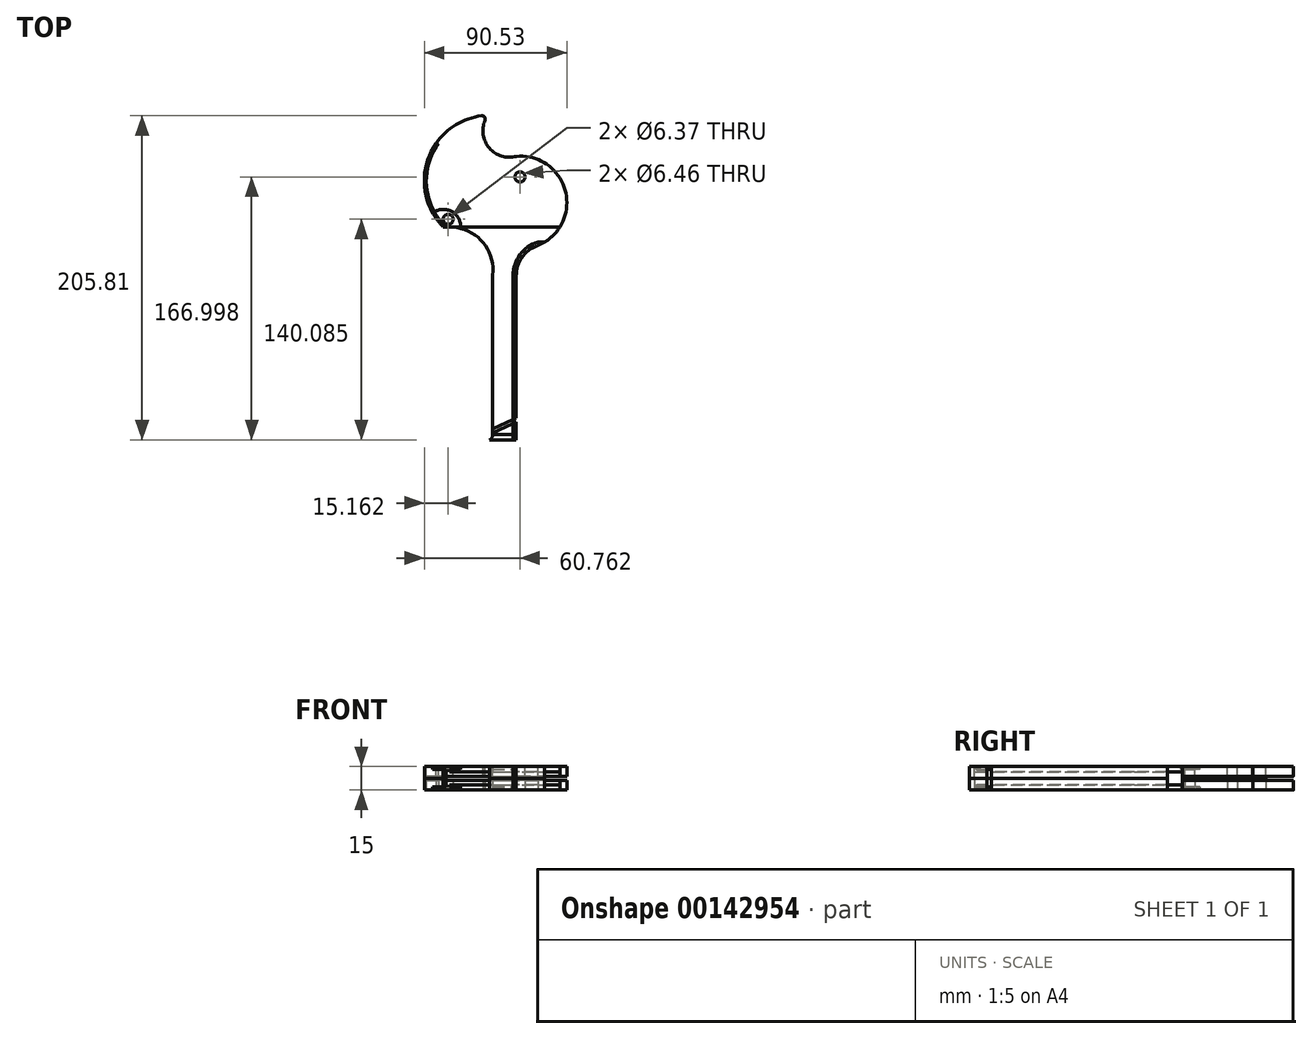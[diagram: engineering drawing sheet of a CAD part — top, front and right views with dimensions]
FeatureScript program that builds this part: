
annotation { "Feature Type Name" : "Feature", "Feature Type Description" : "" }
export const myFeature = defineFeature(function(context is Context, id is Id, definition is map)
    precondition{}
    {
        {
            var Q0;
            Q0=qCreatedBy(makeId("Top.planeOp"),FACE);
            var sketch = newSketch(context, id + "F0", { "sketchPlane" : qUnion([Q0])});
            skLineSegment(sketch, "E0", {"start": v(8.8, -17.92) * mm, "end": v(8.8, -59.13) * mm});
            skArc(sketch, "E1", {"start": v(21.81, 0.82) * mm, "mid": v(40.21, 34.88) * mm, "end": v(8.92, 57.68) * mm});
            skArc(sketch, "E2", {"start": v(-11.05, 80.69) * mm, "mid": v(-8.27, 62.97) * mm, "end": v(8.86, 57.67) * mm});
            skArc(sketch, "E3", {"start": v(-13.14, 83.45) * mm, "mid": v(-47.3, 55.79) * mm, "end": v(-37.55, 12.92) * mm});
            skArc(sketch, "E4", {"start": v(-6.16, -17.65) * mm, "mid": v(-12.98, 3.75) * mm, "end": v(-33.49, 12.92) * mm});
            skLineSegment(sketch, "E5", {"start": v(-6.2, -18.21) * mm, "end": v(-6.2, -119.09) * mm});
            skArc(sketch, "E6", {"start": v(-8.08, -122.34) * mm, "mid": v(-6.7, -120.97) * mm, "end": v(-6.2, -119.09) * mm});
            skLineSegment(sketch, "E7", {"start": v(-8.08, -122.34) * mm, "end": v(8.8, -122.34) * mm});
            skLineSegment(sketch, "E8", {"start": v(8.8, -122.34) * mm, "end": v(8.8, -59.13) * mm});
            skArc(sketch, "E9.filletArc", {"start": v(8.92, 57.68) * mm, "mid": v(8.9, 57.68) * mm, "end": v(8.86, 57.67) * mm});
            skCircle(sketch, "E10", {"center": v(11.17, 44.66) * mm, "radius": 3.23 * mm});
            skCircle(sketch, "E11", {"center": v(-34.43, 17.74) * mm, "radius": 3.19 * mm});
            skPoint(sketch, "E12.visualSharp", {"position": v(8.8, -0.92) * mm});
            skArc(sketch, "E12.filletArc", {"start": v(21.81, 0.82) * mm, "mid": v(12.38, -6.52) * mm, "end": v(8.8, -17.92) * mm});
            skPoint(sketch, "E13.visualSharp", {"position": v(-9.36, 83.75) * mm});
            skArc(sketch, "E13.filletArc", {"start": v(-11.05, 80.69) * mm, "mid": v(-11.3, 82.67) * mm, "end": v(-13.14, 83.45) * mm});
            skPoint(sketch, "E14.visualSharp", {"position": v(-6.2, -17.92) * mm});
            skArc(sketch, "E14.filletArc", {"start": v(-6.16, -17.65) * mm, "mid": v(-6.18, -17.93) * mm, "end": v(-6.2, -18.21) * mm});
            skLineSegment(sketch, "E15", {"start": v(-37.55, 12.92) * mm, "end": v(-33.49, 12.92) * mm});
            skLineSegment(sketch, "E16", {"start": v(-37.55, 12.92) * mm, "end": v(36.55, 12.92) * mm});
            skLineSegment(sketch, "E17.0", {"start": v(6.75, -122.34) * mm, "end": v(6.75, -59.13) * mm});
            skLineSegment(sketch, "E17.1", {"start": v(6.75, -17.92) * mm, "end": v(6.75, -59.13) * mm});
            skArc(sketch, "E17.2", {"start": v(22.5, 3.22) * mm, "mid": v(11.12, -4.74) * mm, "end": v(6.75, -17.92) * mm});
            skLineSegment(sketch, "E18", {"start": v(22.5, 3.22) * mm, "end": v(26.77, 3.22) * mm});
            skArc(sketch, "E19", {"start": v(-40.58, 65.88) * mm, "mid": v(-48.16, 38.5) * mm, "end": v(-35.8, 12.92) * mm});
            skLineSegment(sketch, "E20", {"start": v(-40.58, 65.88) * mm, "end": v(-42.18, 65.88) * mm});
            skLineSegment(sketch, "E21", {"start": v(-6.2, -119.09) * mm, "end": v(6.75, -119.09) * mm});
            skSolve(sketch);
        }
        {
            var Q0;
            Q0=makeQuery(id+"F0.imprint","IMPRINT",FACE,{"disambiguationData":[TD([[makeQuery(id+"F0.imprint","IMPRINT",EDGE,{"derivedFrom":sQuery(id+"F0.wireOp",EDGE,"E0")}),-1.0]])]});
            extrude(context, id + "F1", {"entities" : qUnion([Q0]), "oppositeDirection" : true, "depth" : 7.5 * mm});
        }
        {
            var Q0;
            {var subQ0=sQuery(id+"F0.wireOp",EDGE,"E21");Q0=makeQuery(id+"F0.imprint","IMPRINT",FACE,{"disambiguationData":[TD([[makeQuery(id+"F0.imprint","IMPRINT",EDGE,{"derivedFrom":subQ0}),-1.0]])]});}
            extrude(context, id + "F2", {"entities" : qUnion([Q0]), "oppositeDirection" : true, "depth" : 7.5 * mm});
        }
        {
            var Q0;
            {var subQ1=sQuery(id+"F0.wireOp",EDGE,"E4");Q0=makeQuery(id+"F0.imprint","IMPRINT",FACE,{"disambiguationData":[TD([[makeQuery(id+"F0.imprint","IMPRINT",EDGE,{"derivedFrom":subQ1}),-1.0]])]});}
            extrude(context, id + "F3", {"entities" : qUnion([Q0]), "oppositeDirection" : true, "depth" : 3.33 * mm});
        }
        {
            var Q0;
            Q0=makeQuery(id+"F0.imprint","IMPRINT",FACE,{"disambiguationData":[TD([[makeQuery(id+"F0.imprint","IMPRINT",EDGE,{"derivedFrom":sQuery(id+"F0.wireOp",EDGE,"E2")}),-1.0]])]});
            extrude(context, id + "F4", {"entities" : qUnion([Q0]), "oppositeDirection" : true, "depth" : 6.14 * mm});
        }
        {
            var Q0;
            {var subQ4=sQuery(id+"F0.wireOp",EDGE,"E20");Q0=makeQuery(id+"F0.imprint","IMPRINT",FACE,{"disambiguationData":[TD([[makeQuery(id+"F0.imprint","IMPRINT",EDGE,{"derivedFrom":subQ4}),1.0]])]});}
            extrude(context, id + "F5", {"entities" : qUnion([Q0]), "oppositeDirection" : true, "depth" : 7.5 * mm});
        }
        {
            var Q0;
            Q0=makeQuery(id+"F1.opExtrude","CAP_FACE",FACE,{"disambiguationData":[OSD([sQuery(id+"F0.wireOp",EDGE,"E0"),sQuery(id+"F0.wireOp",EDGE,"E1"),sQuery(id+"F0.wireOp",EDGE,"E7"),sQuery(id+"F0.wireOp",EDGE,"E8"),sQuery(id+"F0.wireOp",EDGE,"E12.filletArc"),sQuery(id+"F0.wireOp",EDGE,"E17.0"),sQuery(id+"F0.wireOp",EDGE,"E17.1"),sQuery(id+"F0.wireOp",EDGE,"E17.2"),sQuery(id+"F0.wireOp",EDGE,"E18")])],"isStart":false});
            cPlane(context, id + "F6", {"entities" : qUnion([Q0]), "cplaneType" : CPlaneType.OFFSET, "offset" : 0 * mm, "width" : 150 * mm, "height" : 150 * mm});
        }
        {
            var Q0;
            Q0=makeQuery(id+"F3.opExtrude","CAP_FACE",FACE,{"disambiguationData":[OSD([sQuery(id+"F0.wireOp",EDGE,"E1"),sQuery(id+"F0.wireOp",EDGE,"E4"),sQuery(id+"F0.wireOp",EDGE,"E5"),sQuery(id+"F0.wireOp",EDGE,"E14.filletArc"),sQuery(id+"F0.wireOp",EDGE,"E16"),sQuery(id+"F0.wireOp",EDGE,"E17.0"),sQuery(id+"F0.wireOp",EDGE,"E17.1"),sQuery(id+"F0.wireOp",EDGE,"E17.2"),sQuery(id+"F0.wireOp",EDGE,"E18"),sQuery(id+"F0.wireOp",EDGE,"E21")])],"isStart":true});
            var sketch = newSketch(context, id + "F7", { "sketchPlane" : qUnion([Q0])});
            skLineSegment(sketch, "E22", {"start": v(-6.2, -118.1) * mm, "end": v(8.8, -111.11) * mm});
            skLineSegment(sketch, "E23", {"start": v(-6.2, -115.32) * mm, "end": v(8.8, -108.33) * mm});
            skLineSegment(sketch, "E24", {"start": v(8.8, -108.33) * mm, "end": v(8.8, -111.11) * mm});
            skSolve(sketch);
        }
        {
            var Q0;
            {var subQ0=sQuery(id+"F7.wireOp",EDGE,"E22");var subQ1=makeQuery(id+"F3.opExtrude","CAP_EDGE",EDGE,{"disambiguationData":[OSD([sQuery(id+"F0.wireOp",EDGE,"E5")])],"isStart":true});var subQ2=makeQuery(id+"F7.imprint","INTERSECT",VERTEX,{"derivedFrom":[subQ1,subQ0]});Q0=makeQuery(id+"F7.imprint","IMPRINT",FACE,{"disambiguationData":[TD([[makeQuery(id+"F7.imprint","IMPRINT",EDGE,{"disambiguationData":[TD([[subQ2,1.0]])],"derivedFrom":subQ1}),1.0]])]});}
            var Q1;
            {var subQ0=sQuery(id+"F7.wireOp",EDGE,"E24");Q1=makeQuery(id+"F7.imprint","IMPRINT",FACE,{"disambiguationData":[TD([[makeQuery(id+"F7.imprint","IMPRINT",EDGE,{"derivedFrom":subQ0}),-1.0]])]});}
            extrude(context, id + "F8", {"entities" : qUnion([Q0, Q1]), "operationType" : NewBodyOperationType.REMOVE, "oppositeDirection" : true, "depth" : 2 * mm});
        }
        {
            var Q0;
            Q0=makeQuery(id+"F1.opExtrude","SWEPT_FACE",FACE,{"disambiguationData":[OSD([sQuery(id+"F0.wireOp",EDGE,"E0"),sQuery(id+"F0.wireOp",EDGE,"E8")])]});
            var sketch = newSketch(context, id + "F9", { "sketchPlane" : qUnion([Q0])});
            skLineSegment(sketch, "E25", {"start": v(-108.33, -2) * mm, "end": v(-108.33, -7.5) * mm});
            skLineSegment(sketch, "E26", {"start": v(-108.33, -7.5) * mm, "end": v(-111.11, -7.5) * mm});
            skLineSegment(sketch, "E27", {"start": v(-111.11, -7.5) * mm, "end": v(-111.11, -2) * mm});
            skSolve(sketch);
        }
        {
            var Q0;
            Q0=makeQuery(id+"F9.imprint","IMPRINT",FACE,{"disambiguationData":[TD([[makeQuery(id+"F9.imprint","IMPRINT",EDGE,{"derivedFrom":sQuery(id+"F9.wireOp",EDGE,"E25")}),-1.0]])]});
            extrude(context, id + "F10", {"entities" : qUnion([Q0]), "operationType" : NewBodyOperationType.REMOVE, "oppositeDirection" : true, "depth" : 2 * mm});
        }
        {
            var Q0;
            Q0=makeQuery(id+"F4.opExtrude","SWEPT_BODY",BODY,{"disambiguationData":[OSD([sQuery(id+"F0.wireOp",EDGE,"E1"),sQuery(id+"F0.wireOp",EDGE,"E2"),sQuery(id+"F0.wireOp",EDGE,"E3"),sQuery(id+"F0.wireOp",EDGE,"E9.filletArc"),sQuery(id+"F0.wireOp",EDGE,"E10"),sQuery(id+"F0.wireOp",EDGE,"E11"),sQuery(id+"F0.wireOp",EDGE,"E13.filletArc"),sQuery(id+"F0.wireOp",EDGE,"E16"),sQuery(id+"F0.wireOp",EDGE,"E19"),sQuery(id+"F0.wireOp",EDGE,"E20")])]});
            var Q1;
            Q1=makeQuery(id+"F3.opExtrude","SWEPT_BODY",BODY,{"disambiguationData":[OSD([sQuery(id+"F0.wireOp",EDGE,"E1"),sQuery(id+"F0.wireOp",EDGE,"E4"),sQuery(id+"F0.wireOp",EDGE,"E5"),sQuery(id+"F0.wireOp",EDGE,"E6"),sQuery(id+"F0.wireOp",EDGE,"E7"),sQuery(id+"F0.wireOp",EDGE,"E14.filletArc"),sQuery(id+"F0.wireOp",EDGE,"E16"),sQuery(id+"F0.wireOp",EDGE,"E17.0"),sQuery(id+"F0.wireOp",EDGE,"E17.1"),sQuery(id+"F0.wireOp",EDGE,"E17.2"),sQuery(id+"F0.wireOp",EDGE,"E18")])]});
            var Q2;
            Q2=makeQuery(id+"F1.opExtrude","SWEPT_BODY",BODY,{"disambiguationData":[OSD([sQuery(id+"F0.wireOp",EDGE,"E0"),sQuery(id+"F0.wireOp",EDGE,"E1"),sQuery(id+"F0.wireOp",EDGE,"E7"),sQuery(id+"F0.wireOp",EDGE,"E8"),sQuery(id+"F0.wireOp",EDGE,"E12.filletArc"),sQuery(id+"F0.wireOp",EDGE,"E17.0"),sQuery(id+"F0.wireOp",EDGE,"E17.1"),sQuery(id+"F0.wireOp",EDGE,"E17.2"),sQuery(id+"F0.wireOp",EDGE,"E18")])]});
            var Q3;
            Q3=makeQuery(id+"F5.opExtrude","SWEPT_BODY",BODY,{"disambiguationData":[OSD([sQuery(id+"F0.wireOp",EDGE,"E3"),sQuery(id+"F0.wireOp",EDGE,"E16"),sQuery(id+"F0.wireOp",EDGE,"E19"),sQuery(id+"F0.wireOp",EDGE,"E20")])]});
            var Q4;
            Q4=makeQuery(id+"F2.opExtrude","SWEPT_BODY",BODY,{"disambiguationData":[OSD([sQuery(id+"F0.wireOp",EDGE,"E6"),sQuery(id+"F0.wireOp",EDGE,"E7"),sQuery(id+"F0.wireOp",EDGE,"E17.0"),sQuery(id+"F0.wireOp",EDGE,"E21")])]});
            var Q5;
            Q5=qCreatedBy(id+"F6.planeOp",FACE);
            mirror(context, id + "F11", {"entities" : qUnion([Q0, Q1, Q2, Q3, Q4]), "mirrorPlane" : qUnion([Q5])});
        }
        {
            var Q0;
            Q0=makeQuery(id+"F4.opExtrude","CAP_FACE",FACE,{"disambiguationData":[OSD([sQuery(id+"F0.wireOp",EDGE,"E1"),sQuery(id+"F0.wireOp",EDGE,"E2"),sQuery(id+"F0.wireOp",EDGE,"E3"),sQuery(id+"F0.wireOp",EDGE,"E9.filletArc"),sQuery(id+"F0.wireOp",EDGE,"E10"),sQuery(id+"F0.wireOp",EDGE,"E11"),sQuery(id+"F0.wireOp",EDGE,"E13.filletArc"),sQuery(id+"F0.wireOp",EDGE,"E16"),sQuery(id+"F0.wireOp",EDGE,"E19"),sQuery(id+"F0.wireOp",EDGE,"E20")])],"isStart":true});
            cPlane(context, id + "F12", {"entities" : qUnion([Q0]), "cplaneType" : CPlaneType.OFFSET, "offset" : 0 * mm, "width" : 150 * mm, "height" : 150 * mm});
        }
        {
            var Q0;
            Q0=qCreatedBy(id+"F12.planeOp",FACE);
            var sketch = newSketch(context, id + "F13", { "sketchPlane" : qUnion([Q0])});
            skArc(sketch, "E28.0", {"start": v(-42.18, 65.88) * mm, "mid": v(-49.44, 38.57) * mm, "end": v(-37.55, 12.92) * mm});
            skLineSegment(sketch, "E29.0", {"start": v(-35.8, 12.92) * mm, "end": v(36.55, 12.92) * mm});
            skArc(sketch, "E30", {"start": v(-26.44, 12.92) * mm, "mid": v(-32.6, 22.87) * mm, "end": v(-44.24, 21.79) * mm});
            skLineSegment(sketch, "E31", {"start": v(-35.8, 12.92) * mm, "end": v(-37.55, 12.92) * mm});
            skArc(sketch, "E32.0", {"start": v(-6.16, -17.65) * mm, "mid": v(-12.98, 3.75) * mm, "end": v(-33.49, 12.92) * mm});
            skLineSegment(sketch, "E33", {"start": v(-26.44, 12.92) * mm, "end": v(-26.44, 12) * mm});
            skSolve(sketch);
        }
        {
            var Q0;
            {var subQ2=sQuery(id+"F13.wireOp",EDGE,"E30");Q0=makeQuery(id+"F13.imprint","IMPRINT",FACE,{"disambiguationData":[TD([[makeQuery(id+"F13.imprint","IMPRINT",EDGE,{"derivedFrom":subQ2}),1.0]])]});}
            var Q1;
            {var subQ3=sQuery(id+"F13.wireOp",EDGE,"E33");Q1=makeQuery(id+"F13.imprint","IMPRINT",FACE,{"disambiguationData":[TD([[makeQuery(id+"F13.imprint","IMPRINT",EDGE,{"derivedFrom":subQ3}),-1.0]])]});}
            extrude(context, id + "F14", {"entities" : qUnion([Q0, Q1]), "operationType" : NewBodyOperationType.REMOVE, "oppositeDirection" : true, "depth" : 2 * mm});
        }
        {
            var Q0;
            Q0=makeQuery(id+"F11.opPattern","COPY",FACE,{"derivedFrom":makeQuery(id+"F4.opExtrude","CAP_FACE",FACE,{"disambiguationData":[OSD([sQuery(id+"F0.wireOp",EDGE,"E1"),sQuery(id+"F0.wireOp",EDGE,"E2"),sQuery(id+"F0.wireOp",EDGE,"E3"),sQuery(id+"F0.wireOp",EDGE,"E9.filletArc"),sQuery(id+"F0.wireOp",EDGE,"E10"),sQuery(id+"F0.wireOp",EDGE,"E11"),sQuery(id+"F0.wireOp",EDGE,"E13.filletArc"),sQuery(id+"F0.wireOp",EDGE,"E16"),sQuery(id+"F0.wireOp",EDGE,"E19"),sQuery(id+"F0.wireOp",EDGE,"E20")])],"isStart":true}),"instanceName":"1"});
            cPlane(context, id + "F15", {"entities" : qUnion([Q0]), "cplaneType" : CPlaneType.OFFSET, "offset" : 0 * mm, "width" : 150 * mm, "height" : 150 * mm});
        }
        {
            var Q0;
            Q0=qCreatedBy(id+"F15.planeOp",FACE);
            var sketch = newSketch(context, id + "F16", { "sketchPlane" : qUnion([Q0])});
            skLineSegment(sketch, "E34.0", {"start": v(-35.8, -12.92) * mm, "end": v(36.55, -12.92) * mm});
            skArc(sketch, "E35.0", {"start": v(-42.18, -65.88) * mm, "mid": v(-49.44, -38.57) * mm, "end": v(-37.55, -12.92) * mm});
            skLineSegment(sketch, "E36.0", {"start": v(-37.55, -12.92) * mm, "end": v(-35.8, -12.92) * mm});
            skArc(sketch, "E37.0", {"start": v(-6.16, 17.65) * mm, "mid": v(-12.98, -3.75) * mm, "end": v(-33.49, -12.92) * mm});
            skArc(sketch, "E38", {"start": v(-44.24, -21.79) * mm, "mid": v(-32.6, -22.87) * mm, "end": v(-26.44, -12.92) * mm});
            skLineSegment(sketch, "E39", {"start": v(-26.44, -12.92) * mm, "end": v(-26.44, -12) * mm});
            skSolve(sketch);
        }
        {
            var Q0;
            {var subQ3=sQuery(id+"F16.wireOp",EDGE,"E39");Q0=makeQuery(id+"F16.imprint","IMPRINT",FACE,{"disambiguationData":[TD([[makeQuery(id+"F16.imprint","IMPRINT",EDGE,{"derivedFrom":subQ3}),1.0]])]});}
            var Q1;
            {var subQ0=sQuery(id+"F16.wireOp",EDGE,"E36.0");Q1=makeQuery(id+"F16.imprint","IMPRINT",FACE,{"disambiguationData":[TD([[makeQuery(id+"F16.imprint","IMPRINT",EDGE,{"derivedFrom":subQ0}),-1.0]])]});}
            extrude(context, id + "F17", {"entities" : qUnion([Q0, Q1]), "operationType" : NewBodyOperationType.REMOVE, "oppositeDirection" : true, "depth" : 2 * mm});
        }
    });
